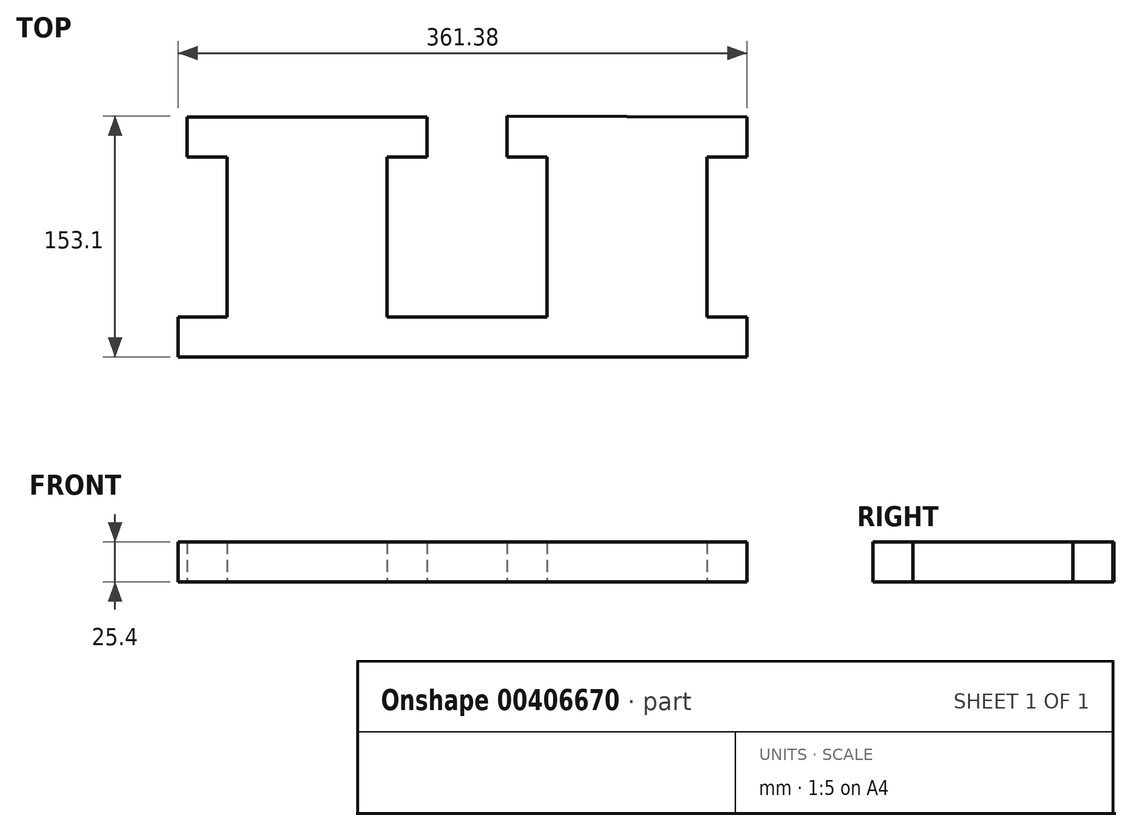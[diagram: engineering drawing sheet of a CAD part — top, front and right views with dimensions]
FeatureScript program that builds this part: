
annotation { "Feature Type Name" : "Feature", "Feature Type Description" : "" }
export const myFeature = defineFeature(function(context is Context, id is Id, definition is map)
    precondition{}
    {
        {
            var Q0;
            Q0=qCreatedBy(makeId("Top.planeOp"),FACE);
            var sketch = newSketch(context, id + "F0", { "sketchPlane" : qUnion([Q0])});
            skLineSegment(sketch, "E0.bottom", {"start": v(50.8, -50.8) * mm, "end": v(-50.8, -50.8) * mm});
            skLineSegment(sketch, "E0.top", {"start": v(50.8, 50.8) * mm, "end": v(25.4, 50.8) * mm});
            skLineSegment(sketch, "E0.left", {"start": v(50.8, -50.8) * mm, "end": v(50.8, 50.8) * mm});
            skLineSegment(sketch, "E0.right", {"start": v(-50.8, -50.8) * mm, "end": v(-50.8, 50.8) * mm});
            skPoint(sketch, "E0.middle", {"position": v(0, 0) * mm});
            skLineSegment(sketch, "E1", {"start": v(-25.4, 50.8) * mm, "end": v(-25.4, 76.2) * mm});
            skLineSegment(sketch, "E2", {"start": v(25.4, 50.8) * mm, "end": v(25.4, 76.9) * mm});
            skPoint(sketch, "E3.start.orphan", {"position": v(0, 36.4) * mm});
            skLineSegment(sketch, "E4.trimOffspring", {"start": v(-23.7, 50.8) * mm, "end": v(-50.8, 50.8) * mm});
            skLineSegment(sketch, "E5.right", {"start": v(-152.4, -50.8) * mm, "end": v(-152.4, 50.8) * mm});
            skPoint(sketch, "E5.middle", {"position": v(-50.8, 0) * mm});
            skLineSegment(sketch, "E6", {"start": v(-152.4, 50.8) * mm, "end": v(-177.8, 50.8) * mm});
            skLineSegment(sketch, "E7", {"start": v(-177.8, 50.8) * mm, "end": v(-177.8, 76.2) * mm});
            skLineSegment(sketch, "E8", {"start": v(-177.8, 76.2) * mm, "end": v(-76.2, 76.2) * mm});
            skLineSegment(sketch, "E9", {"start": v(-76.2, 76.2) * mm, "end": v(-25.4, 76.2) * mm});
            skLineSegment(sketch, "E10", {"start": v(-25.4, 101.6) * mm, "end": v(-76.2, 101.6) * mm});
            skLineSegment(sketch, "E11", {"start": v(25.4, 101.6) * mm, "end": v(76.2, 101.6) * mm});
            skLineSegment(sketch, "E12", {"start": v(-25.4, 101.6) * mm, "end": v(25.4, 101.6) * mm});
            skLineSegment(sketch, "E13", {"start": v(-76.2, 101.6) * mm, "end": v(-76.2, 76.2) * mm});
            skLineSegment(sketch, "E14", {"start": v(152.4, 50.8) * mm, "end": v(152.4, -50.8) * mm});
            skLineSegment(sketch, "E15", {"start": v(152.4, 50.8) * mm, "end": v(177.8, 50.8) * mm});
            skLineSegment(sketch, "E16", {"start": v(177.8, 50.8) * mm, "end": v(177.8, 76.2) * mm});
            skPoint(sketch, "E17.end.orphan", {"position": v(134.28, 77.6) * mm});
            skLineSegment(sketch, "E18", {"start": v(25.4, 76.9) * mm, "end": v(177.8, 76.2) * mm});
            skLineSegment(sketch, "E19", {"start": v(152.4, -50.8) * mm, "end": v(254, -50.8) * mm});
            skLineSegment(sketch, "E20", {"start": v(228.6, 101.6) * mm, "end": v(239.26, 101.6) * mm});
            skLineSegment(sketch, "E21", {"start": v(228.6, 63.5) * mm, "end": v(228.6, 101.6) * mm});
            skLineSegment(sketch, "E22", {"start": v(228.6, 63.5) * mm, "end": v(228.6, 49.84) * mm});
            skLineSegment(sketch, "E23", {"start": v(228.6, 50.16) * mm, "end": v(254, 49.84) * mm});
            skLineSegment(sketch, "E24", {"start": v(254, 49.84) * mm, "end": v(254, -50.8) * mm});
            skPoint(sketch, "E25.start.orphan", {"position": v(177.8, 63.5) * mm});
            skPoint(sketch, "E26.end.orphan", {"position": v(76.2, 77.6) * mm});
            skLineSegment(sketch, "E27", {"start": v(76.2, 101.6) * mm, "end": v(228.6, 101.6) * mm});
            skLineSegment(sketch, "E28", {"start": v(-152.4, -50.8) * mm, "end": v(-183.58, -50.8) * mm});
            skLineSegment(sketch, "E29", {"start": v(-183.58, -50.8) * mm, "end": v(-183.58, -76.2) * mm});
            skLineSegment(sketch, "E30", {"start": v(-183.58, -76.2) * mm, "end": v(177.8, -76.2) * mm});
            skPoint(sketch, "E31.endSnap0", {"position": v(203.2, -50.8) * mm});
            skLineSegment(sketch, "E32", {"start": v(177.8, -50.8) * mm, "end": v(177.8, -76.2) * mm});
            skSolve(sketch);
        }
        {
            var Q0;
            {var subQ1=sQuery(id+"F0.wireOp",EDGE,"E0.right");Q0=makeQuery(id+"F0.imprint","IMPRINT",FACE,{"disambiguationData":[TD([[makeQuery(id+"F0.imprint","IMPRINT",EDGE,{"derivedFrom":subQ1}),1.0]])]});}
            extrude(context, id + "F1", {"entities" : qUnion([Q0]), "depth" : 25.4 * mm, "offsetDistance" : 25.4 * mm});
        }
    });
